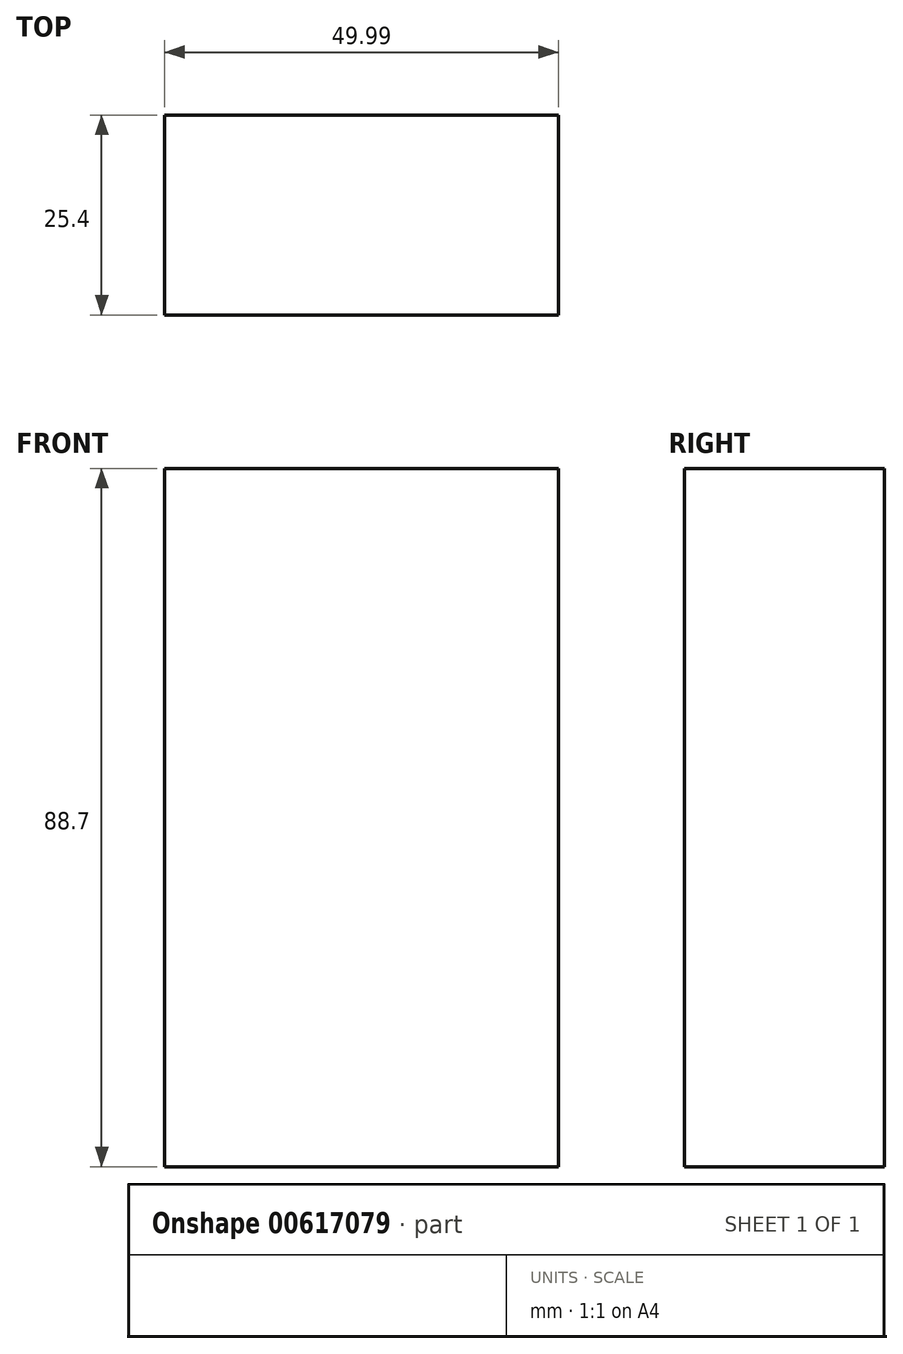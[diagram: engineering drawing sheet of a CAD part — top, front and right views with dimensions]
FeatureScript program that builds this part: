
annotation { "Feature Type Name" : "Feature", "Feature Type Description" : "" }
export const myFeature = defineFeature(function(context is Context, id is Id, definition is map)
    precondition{}
    {
        {
            var Q0;
            Q0=qCreatedBy(makeId("Front.planeOp"),FACE);
            var sketch = newSketch(context, id + "F0", { "sketchPlane" : qUnion([Q0])});
            skLineSegment(sketch, "E0", {"start": v(-33.68, 32.92) * mm, "end": v(-33.68, -55.78) * mm});
            skLineSegment(sketch, "E1", {"start": v(-33.68, 32.92) * mm, "end": v(16.3, 32.92) * mm});
            skLineSegment(sketch, "E2", {"start": v(16.3, 32.92) * mm, "end": v(16.3, -55.78) * mm});
            skLineSegment(sketch, "E3", {"start": v(-33.68, -55.78) * mm, "end": v(16.3, -55.78) * mm});
            skSolve(sketch);
        }
        {
            var Q0;
            Q0 = qSketchRegion(id + "F0", true);
            extrude(context, id + "F1", {"entities" : qUnion([Q0]), "depth" : 25.4 * mm, "offsetDistance" : 25.4 * mm});
        }
    });
